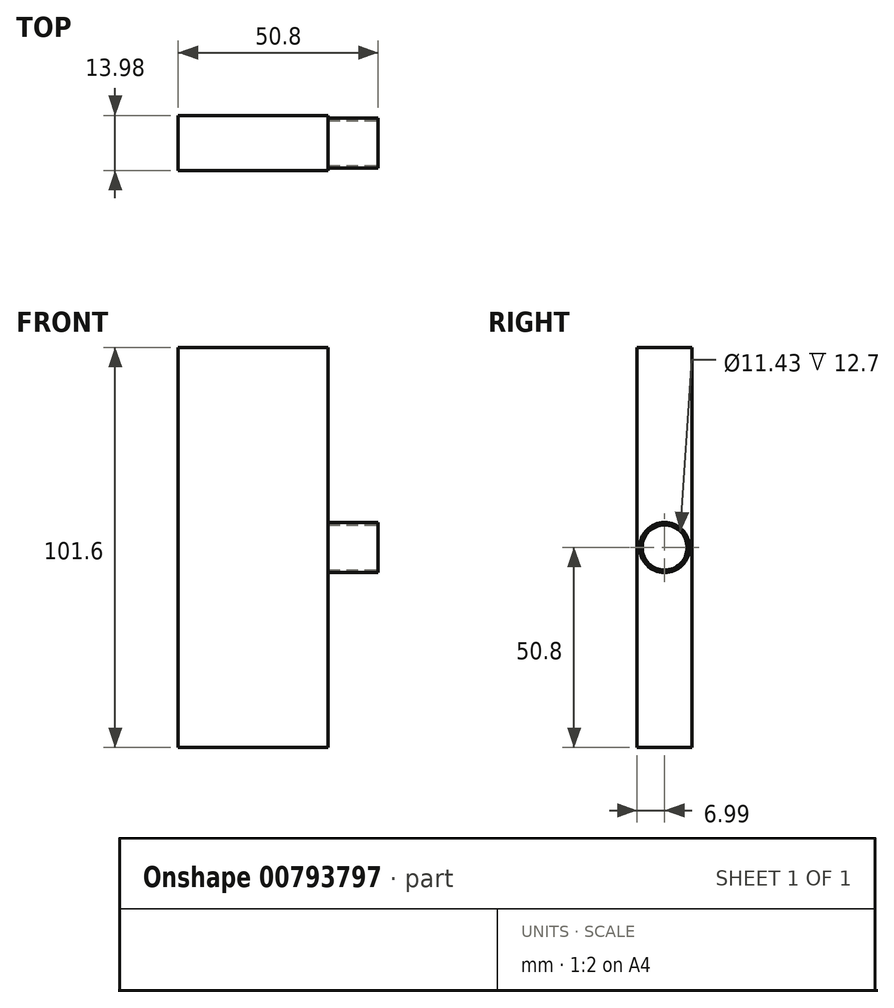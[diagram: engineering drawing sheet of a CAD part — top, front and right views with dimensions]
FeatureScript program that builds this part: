
annotation { "Feature Type Name" : "Feature", "Feature Type Description" : "" }
export const myFeature = defineFeature(function(context is Context, id is Id, definition is map)
    precondition{}
    {
        {
            var Q0;
            Q0=qCreatedBy(makeId("Right.planeOp"),FACE);
            var sketch = newSketch(context, id + "F0", { "sketchPlane" : qUnion([Q0])});
            skCircle(sketch, "E0", {"center": v(0, 0) * mm, "radius": 6.35 * mm});
            skSolve(sketch);
        }
        {
            var Q0;
            Q0 = qSketchRegion(id + "F0", true);
            extrude(context, id + "F1", {"entities" : qUnion([Q0]), "oppositeDirection" : true, "depth" : 12.7 * mm, "offsetDistance" : 25.4 * mm});
        }
        {
            var Q0;
            Q0=makeQuery(id+"F1.opExtrude","CAP_FACE",FACE,{"disambiguationData":[OSD([sQuery(id+"F0.wireOp",EDGE,"E0")])],"isStart":false});
            var sketch = newSketch(context, id + "F2", { "sketchPlane" : qUnion([Q0])});
            skLineSegment(sketch, "E1.bottom", {"start": v(-6.98, 50.8) * mm, "end": v(6.99, 50.8) * mm});
            skLineSegment(sketch, "E1.top", {"start": v(-6.99, -50.8) * mm, "end": v(6.98, -50.8) * mm});
            skLineSegment(sketch, "E1.left", {"start": v(-6.98, 50.8) * mm, "end": v(-6.99, -50.8) * mm});
            skLineSegment(sketch, "E1.right", {"start": v(6.99, 50.8) * mm, "end": v(6.98, -50.8) * mm});
            skPoint(sketch, "E1.middle", {"position": v(0, 0) * mm});
            skSolve(sketch);
        }
        {
            var Q0;
            Q0 = qSketchRegion(id + "F2", true);
            extrude(context, id + "F3", {"entities" : qUnion([Q0]), "operationType" : NewBodyOperationType.ADD, "depth" : 38.1 * mm, "offsetDistance" : 25.4 * mm});
        }
        {
            var Q0;
            Q0=makeQuery(id+"F1.opExtrude","CAP_FACE",FACE,{"disambiguationData":[OSD([sQuery(id+"F0.wireOp",EDGE,"E0")])],"isStart":true});
            var sketch = newSketch(context, id + "F4", { "sketchPlane" : qUnion([Q0])});
            skCircle(sketch, "E2", {"center": v(0, 0) * mm, "radius": 5.72 * mm});
            skSolve(sketch);
        }
        {
            var Q0;
            Q0 = qSketchRegion(id + "F4", true);
            extrude(context, id + "F5", {"entities" : qUnion([Q0]), "operationType" : NewBodyOperationType.REMOVE, "oppositeDirection" : true, "depth" : 12.7 * mm, "offsetDistance" : 25.4 * mm});
        }
    });
